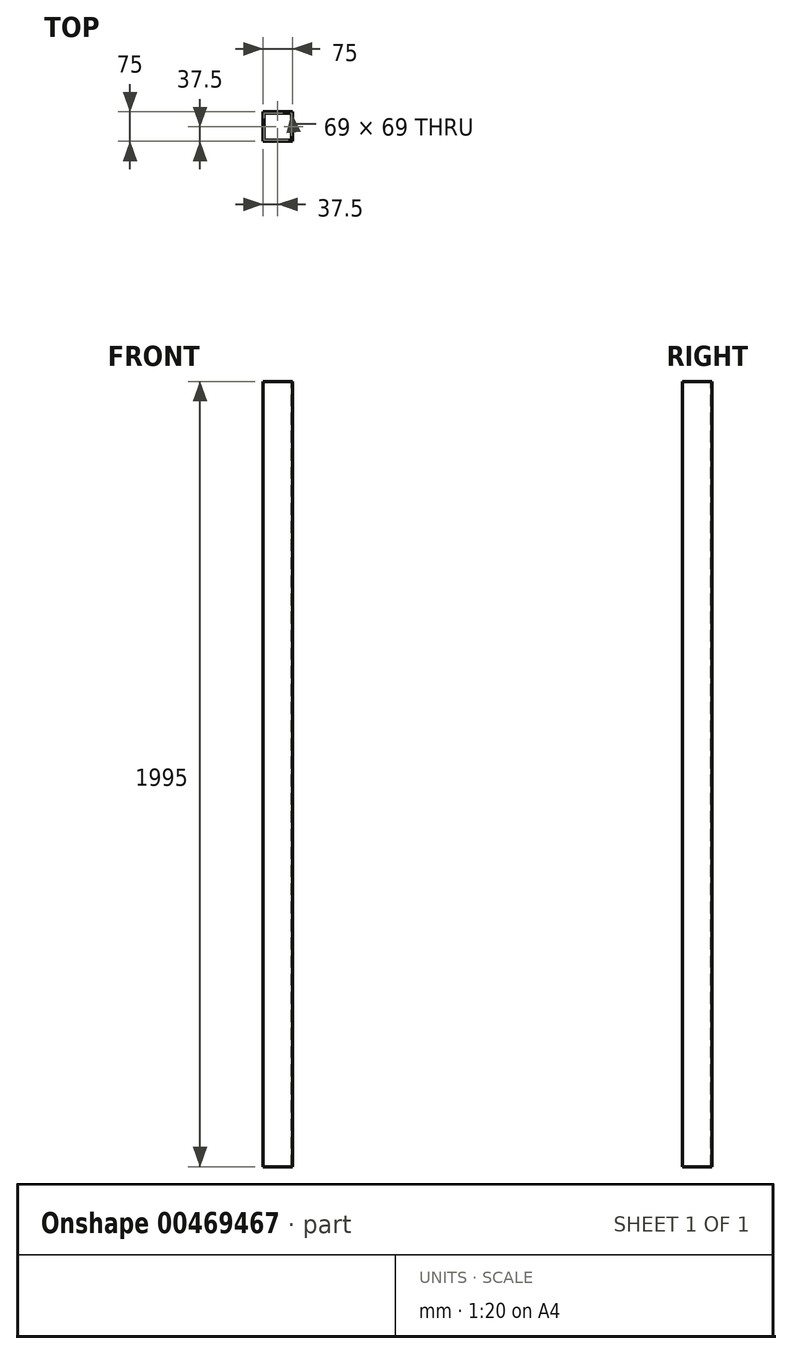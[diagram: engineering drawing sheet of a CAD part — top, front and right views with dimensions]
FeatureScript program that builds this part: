
annotation { "Feature Type Name" : "Feature", "Feature Type Description" : "" }
export const myFeature = defineFeature(function(context is Context, id is Id, definition is map)
    precondition{}
    {
        {
            var Q0;
            Q0=qCreatedBy(makeId("Top.planeOp"),FACE);
            var sketch = newSketch(context, id + "F0", { "sketchPlane" : qUnion([Q0])});
            skLineSegment(sketch, "E0.bottom", {"start": v(0, 0) * mm, "end": v(75, 0) * mm});
            skLineSegment(sketch, "E0.top", {"start": v(0, -75) * mm, "end": v(75, -75) * mm});
            skLineSegment(sketch, "E0.left", {"start": v(0, 0) * mm, "end": v(0, -75) * mm});
            skLineSegment(sketch, "E0.right", {"start": v(75, 0) * mm, "end": v(75, -75) * mm});
            skSolve(sketch);
        }
        {
            var Q0;
            Q0 = qSketchRegion(id + "F0", true);
            extrude(context, id + "F1", {"entities" : qUnion([Q0]), "depth" : 1995 * mm});
        }
        {
            var Q0;
            Q0=makeQuery(id+"F1.opExtrude","CAP_FACE",FACE,{"disambiguationData":[OSD([sQuery(id+"F0.wireOp",EDGE,"E0.bottom"),sQuery(id+"F0.wireOp",EDGE,"E0.top"),sQuery(id+"F0.wireOp",EDGE,"E0.left"),sQuery(id+"F0.wireOp",EDGE,"E0.right")])],"isStart":false});
            var sketch = newSketch(context, id + "F2", { "sketchPlane" : qUnion([Q0])});
            skLineSegment(sketch, "E1.bottom", {"start": v(3, -3) * mm, "end": v(72, -3) * mm});
            skLineSegment(sketch, "E1.top", {"start": v(3, -72) * mm, "end": v(72, -72) * mm});
            skLineSegment(sketch, "E1.left", {"start": v(3, -3) * mm, "end": v(3, -72) * mm});
            skLineSegment(sketch, "E1.right", {"start": v(72, -3) * mm, "end": v(72, -72) * mm});
            skSolve(sketch);
        }
        {
            var Q0;
            Q0=makeQuery(id+"F2.imprint","IMPRINT",FACE,{"disambiguationData":[TD([[makeQuery(id+"F2.imprint","IMPRINT",EDGE,{"derivedFrom":sQuery(id+"F2.wireOp",EDGE,"E1.bottom")}),-1.0]])]});
            extrude(context, id + "F3", {"entities" : qUnion([Q0]), "operationType" : NewBodyOperationType.REMOVE, "endBound" : BoundingType.THROUGH_ALL, "oppositeDirection" : true, "depth" : -1995 * mm});
        }
    });
